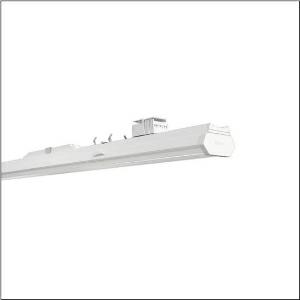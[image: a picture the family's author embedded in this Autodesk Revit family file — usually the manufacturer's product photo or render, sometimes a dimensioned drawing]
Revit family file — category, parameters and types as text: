
# Revit family: licross_11_protected_ho_51tp13dn4f5s
name_source: partatom
category: Lighting Fixtures
units: mm (PartAtom-declared; Revit-internal decimal feet)

## family parameters
Cut with Voids When Loaded = No
Host = Face
Light Source = No
Part Type = Normal
Room Calculation Point = No
Round Connector Dimension = Use Diameter
Shared = No

## types (1)
- --- (1 x LED, 15550 lm, 87.3 W, 4000K)
    Apparent Load = 87 VA
    CIE Flux Codes = 89 96 99 100 99
    Color Rendering = 80
    Color Temperature = 4000K
    Default Elevation = 1800 mm
    Description = Licross 11 Protected HO, luminaire insert, of sheet steel, galvanised, coil coated, white, length: 1.500mm, width: 90mm, height: 101mm, LED rated luminous flux: 15.550lm, light colour: 840, SDCM (Standard Deviation of Colour Matching)MacAdam ≤ 2 SDCM (initial), control gear: DALI 2, with plug, 5-pole, with phase selection, mains connection: 220..240V, AC, 50/60Hz, rated input power: 87W, internal wiring halogen-free, primary light control with lens, of plastic, primary optical cover: cover, of PMMA, light emission: direct distribution, primary light characteristic: symmetric, protection rating (complete): IP64, insulation class (complete): insulation class I (protective earthing), certification: CE, ENEC, VDE, UKCA, protection symbol: D if used in an environment with conductive dust loads with corresponding accessories, impact resistance: IK06, permissible ambient temperature for indoor applications: -25..+30°C, corresponds to IFS (International Featured Standards) requirements for safety and quality in the food industry, reducing of maximum allowable ambient temperature of 5°C with ceiling mounting, LABS conformity tested according to VDMA 24364:2018-05, The light source and the operating device comply with the requirements of the Ecodesign Regulation (EU) 2019/2020 and are replaceable in accordance with this regulation, packaging unit: 1 piece
    Height = 92 mm
    Lamp = 1 x LED
    Lamp Light Flux = 15550 lm
    Lamp Power = 87.3 W
    Lamp count = 1
    Length = 1500 mm
    Luminous efficacy = 178 lm/W
    Manufacturer = Siteco
    ModVariant = No
    Model = 51TP13DN4F5S
    Mounting Place = Ceiling
    Mounting Type = Pendant
    Number of Poles = 1
    OnlyDefault = Yes
    Power Factor = 1
    Product Name = Licross 11 Protected HO
    Product group = luminaire insert | ceiling pendant
    ProductGroupID = 901
    Protection Class = Protection class I
    Protection Degree = IP 64
    RLX_Detail_Level = 1
    RLX_Emergency_Light_Flux = 0 lm
    RLX_Emergency_Type = 0
    RLX_Emergency_Type_DB = No
    RlxData = <blob elided: 24549 chars, md5=3680c1fe>
    Socket = socket
    Standby Power = 0 W
    System Light Flux = 15550 lm
    System Power = 87 W
    Type Comments = factory setting: luminous flux: 100 % | dim-lin: 254 | 589 mA
    Type Image = l_1256148.jpg
    URL = http://relux.com
    VarID = @adj_102431
    Voltage = 0 V
    Weight = 0.00 kg
    Width = 88 mm

## geometry (parser evidence)
native form markers: Blend x4, Sweep x12
no freeform markers — native parametric forms only
